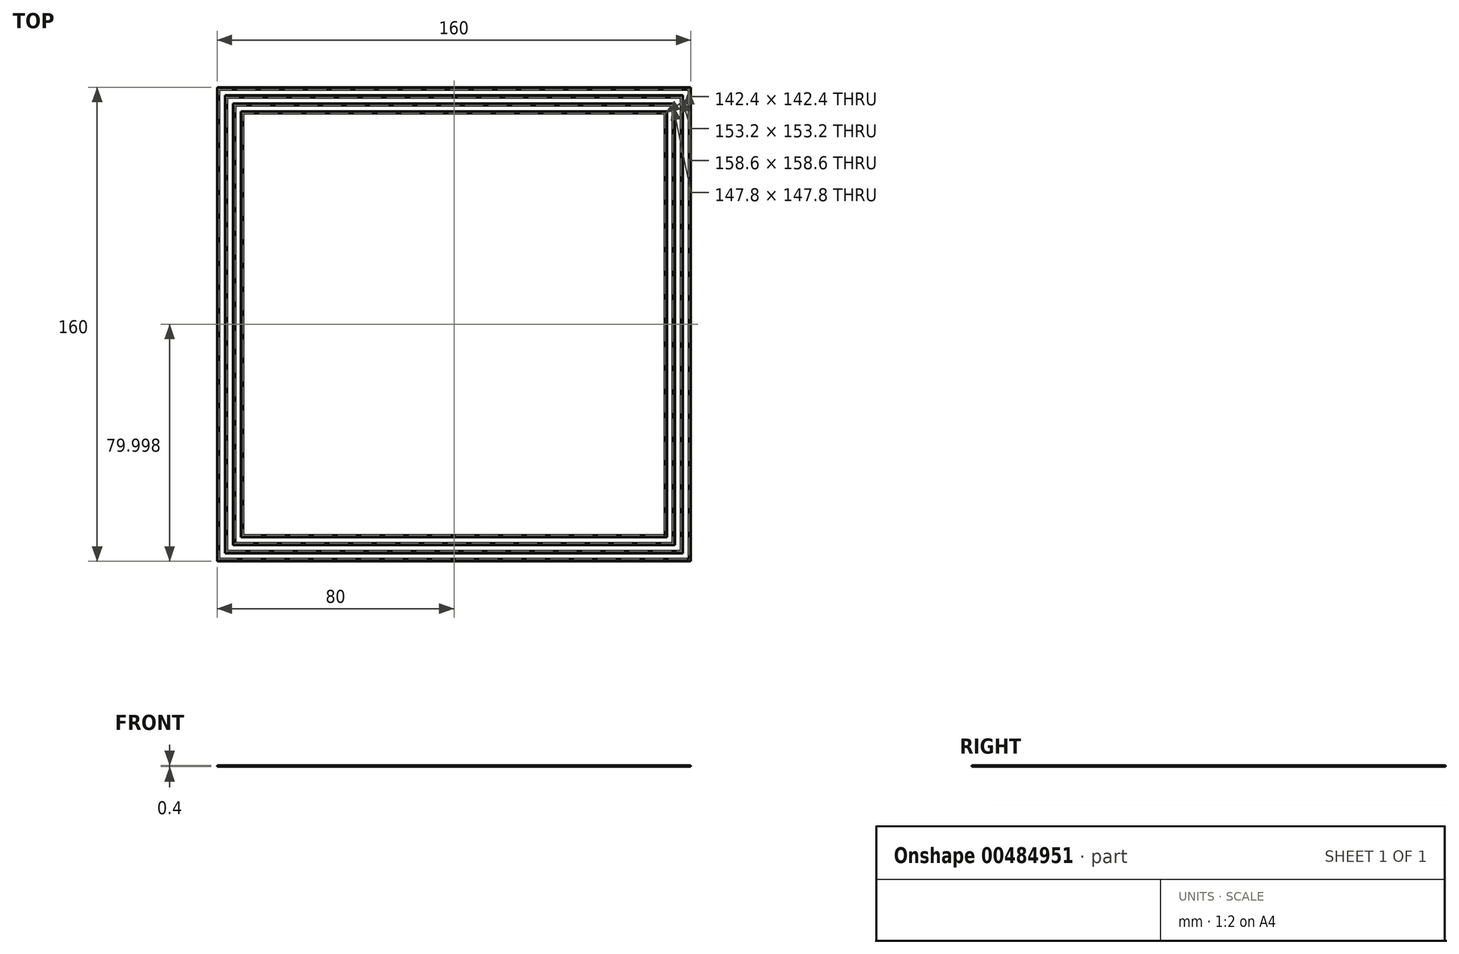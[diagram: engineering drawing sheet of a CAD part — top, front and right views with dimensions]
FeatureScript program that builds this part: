
annotation { "Feature Type Name" : "Feature", "Feature Type Description" : "" }
export const myFeature = defineFeature(function(context is Context, id is Id, definition is map)
    precondition{}
    {
        {
            var Q0;
            Q0=qCreatedBy(makeId("Top.planeOp"),FACE);
            var sketch = newSketch(context, id + "F0", { "sketchPlane" : qUnion([Q0])});
            skLineSegment(sketch, "E0.bottom", {"start": v(80, -65.64) * mm, "end": v(-80, -65.64) * mm});
            skLineSegment(sketch, "E0.top", {"start": v(80, 94.36) * mm, "end": v(-80, 94.36) * mm});
            skLineSegment(sketch, "E0.left", {"start": v(80, -65.64) * mm, "end": v(80, 94.36) * mm});
            skLineSegment(sketch, "E0.right", {"start": v(-80, -65.64) * mm, "end": v(-80, 94.36) * mm});
            skPoint(sketch, "E0.middle", {"position": v(0, 14.36) * mm});
            skLineSegment(sketch, "E1.bottom", {"start": v(79.3, -64.94) * mm, "end": v(-79.3, -64.94) * mm});
            skLineSegment(sketch, "E1.top", {"start": v(79.3, 93.66) * mm, "end": v(-79.3, 93.66) * mm});
            skLineSegment(sketch, "E1.left", {"start": v(79.3, -64.94) * mm, "end": v(79.3, 93.66) * mm});
            skLineSegment(sketch, "E1.right", {"start": v(-79.3, -64.94) * mm, "end": v(-79.3, 93.66) * mm});
            skLineSegment(sketch, "E2.bottom", {"start": v(77.3, -62.94) * mm, "end": v(-77.3, -62.94) * mm});
            skLineSegment(sketch, "E2.top", {"start": v(77.3, 91.66) * mm, "end": v(-77.3, 91.66) * mm});
            skLineSegment(sketch, "E2.left", {"start": v(77.3, -62.94) * mm, "end": v(77.3, 91.66) * mm});
            skLineSegment(sketch, "E2.right", {"start": v(-77.3, -62.94) * mm, "end": v(-77.3, 91.66) * mm});
            skLineSegment(sketch, "E3.bottom", {"start": v(76.6, -62.24) * mm, "end": v(-76.6, -62.24) * mm});
            skLineSegment(sketch, "E3.top", {"start": v(76.6, 90.96) * mm, "end": v(-76.6, 90.96) * mm});
            skLineSegment(sketch, "E3.left", {"start": v(76.6, -62.24) * mm, "end": v(76.6, 90.96) * mm});
            skLineSegment(sketch, "E3.right", {"start": v(-76.6, -62.24) * mm, "end": v(-76.6, 90.96) * mm});
            skLineSegment(sketch, "E4.bottom", {"start": v(74.6, -60.24) * mm, "end": v(-74.6, -60.24) * mm});
            skLineSegment(sketch, "E4.top", {"start": v(74.6, 88.96) * mm, "end": v(-74.6, 88.96) * mm});
            skLineSegment(sketch, "E4.left", {"start": v(74.6, -60.24) * mm, "end": v(74.6, 88.96) * mm});
            skLineSegment(sketch, "E4.right", {"start": v(-74.6, -60.24) * mm, "end": v(-74.6, 88.96) * mm});
            skLineSegment(sketch, "E5.bottom", {"start": v(73.9, -59.54) * mm, "end": v(-73.9, -59.54) * mm});
            skLineSegment(sketch, "E5.top", {"start": v(73.9, 88.26) * mm, "end": v(-73.9, 88.26) * mm});
            skLineSegment(sketch, "E5.left", {"start": v(73.9, -59.54) * mm, "end": v(73.9, 88.26) * mm});
            skLineSegment(sketch, "E5.right", {"start": v(-73.9, -59.54) * mm, "end": v(-73.9, 88.26) * mm});
            skLineSegment(sketch, "E6.bottom", {"start": v(71.9, -57.54) * mm, "end": v(-71.9, -57.54) * mm});
            skLineSegment(sketch, "E6.top", {"start": v(71.9, 86.26) * mm, "end": v(-71.9, 86.26) * mm});
            skLineSegment(sketch, "E6.left", {"start": v(71.9, -57.54) * mm, "end": v(71.9, 86.26) * mm});
            skLineSegment(sketch, "E6.right", {"start": v(-71.9, -57.54) * mm, "end": v(-71.9, 86.26) * mm});
            skLineSegment(sketch, "E7.bottom", {"start": v(71.2, -56.84) * mm, "end": v(-71.2, -56.84) * mm});
            skLineSegment(sketch, "E7.top", {"start": v(71.2, 85.56) * mm, "end": v(-71.2, 85.56) * mm});
            skLineSegment(sketch, "E7.left", {"start": v(71.2, -56.84) * mm, "end": v(71.2, 85.56) * mm});
            skLineSegment(sketch, "E7.right", {"start": v(-71.2, -56.84) * mm, "end": v(-71.2, 85.56) * mm});
            skSolve(sketch);
        }
        {
            var Q0;
            Q0=makeQuery(id+"F0.imprint","IMPRINT",FACE,{"disambiguationData":[TD([[makeQuery(id+"F0.imprint","IMPRINT",EDGE,{"derivedFrom":sQuery(id+"F0.wireOp",EDGE,"E0.bottom")}),-1.0]])]});
            var Q1;
            Q1=makeQuery(id+"F0.imprint","IMPRINT",FACE,{"disambiguationData":[TD([[makeQuery(id+"F0.imprint","IMPRINT",EDGE,{"derivedFrom":sQuery(id+"F0.wireOp",EDGE,"E2.bottom")}),-1.0]])]});
            var Q2;
            Q2=makeQuery(id+"F0.imprint","IMPRINT",FACE,{"disambiguationData":[TD([[makeQuery(id+"F0.imprint","IMPRINT",EDGE,{"derivedFrom":sQuery(id+"F0.wireOp",EDGE,"E4.bottom")}),-1.0]])]});
            var Q3;
            Q3=makeQuery(id+"F0.imprint","IMPRINT",FACE,{"disambiguationData":[TD([[makeQuery(id+"F0.imprint","IMPRINT",EDGE,{"derivedFrom":sQuery(id+"F0.wireOp",EDGE,"E6.bottom")}),-1.0]])]});
            extrude(context, id + "F1", {"entities" : qUnion([Q0, Q1, Q2, Q3]), "depth" : .4 * mm});
        }
    });
